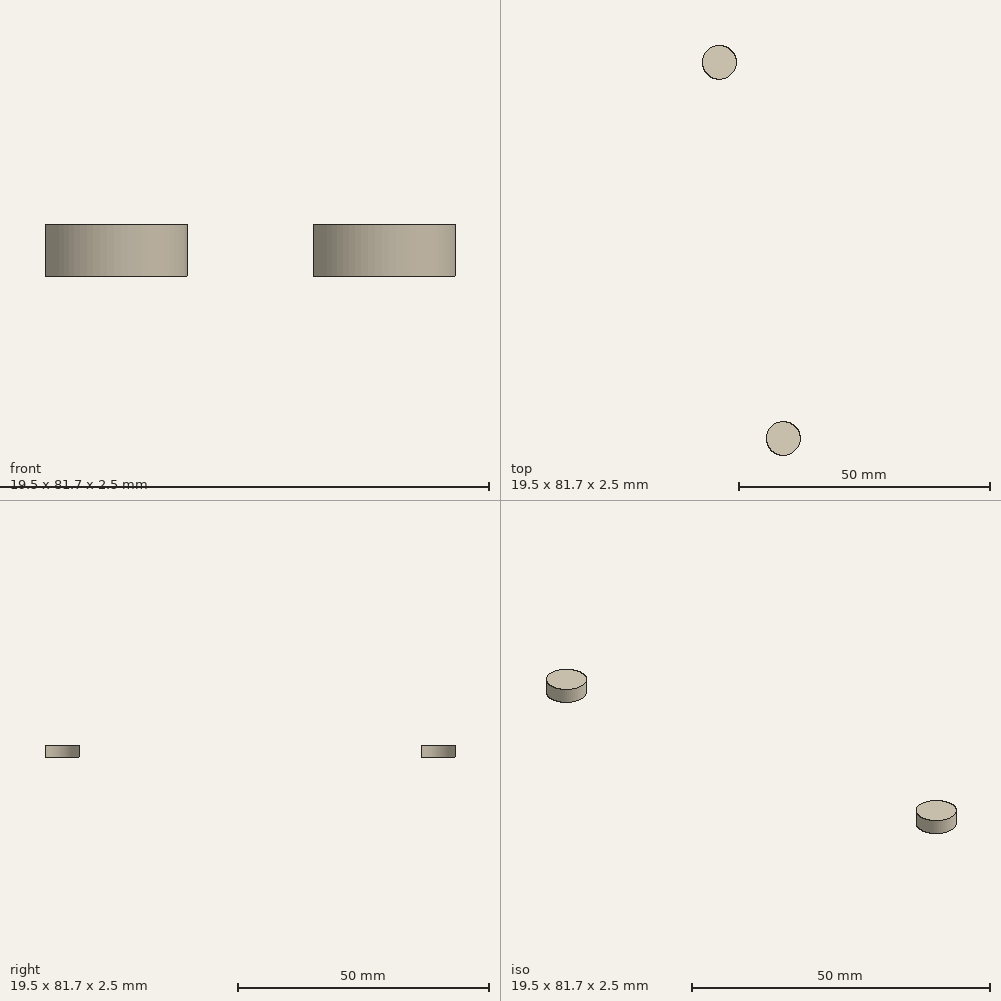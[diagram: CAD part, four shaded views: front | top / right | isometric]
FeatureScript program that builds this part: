
annotation { "Feature Type Name" : "Feature", "Feature Type Description" : "" }
export const myFeature = defineFeature(function(context is Context, id is Id, definition is map)
    precondition{}
    {
        {
            var Q0;
            Q0=qCreatedBy(makeId("Top.planeOp"),FACE);
            var sketch = newSketch(context, id + "F0", { "sketchPlane" : qUnion([Q0])});
            skLineSegment(sketch, "E0", {"start": v(0, 60) * mm, "end": v(0, -60) * mm});
            skLineSegment(sketch, "E1", {"start": v(-70, 0) * mm, "end": v(70, 0) * mm});
            skCircle(sketch, "E2", {"center": v(-12.25, -50) * mm, "radius": 3.37 * mm});
            skCircle(sketch, "E3", {"center": v(12.25, -50) * mm, "radius": 3.37 * mm});
            skCircle(sketch, "E4", {"center": v(-25, -25) * mm, "radius": 3.37 * mm});
            skCircle(sketch, "E5", {"center": v(-25, 0) * mm, "radius": 3.37 * mm});
            skCircle(sketch, "E6", {"center": v(-25, 25) * mm, "radius": 3.37 * mm});
            skCircle(sketch, "E7", {"center": v(-25, 50) * mm, "radius": 3.37 * mm});
            skCircle(sketch, "E8", {"center": v(25, -25) * mm, "radius": 3.37 * mm});
            skCircle(sketch, "E9", {"center": v(25, 0) * mm, "radius": 3.37 * mm});
            skCircle(sketch, "E10", {"center": v(25, 25) * mm, "radius": 3.37 * mm});
            skCircle(sketch, "E11", {"center": v(25, 50) * mm, "radius": 3.37 * mm});
            skLineSegment(sketch, "E12", {"start": v(50, -75) * mm, "end": v(-50, -75) * mm});
            skLineSegment(sketch, "E13", {"start": v(-50, 75) * mm, "end": v(-50, -75) * mm});
            skLineSegment(sketch, "E14", {"start": v(-50, 75) * mm, "end": v(50, 75) * mm});
            skLineSegment(sketch, "E15", {"start": v(50, 75) * mm, "end": v(50, -75) * mm});
            skSolve(sketch);
        }
        {
            var Q0;
            Q0=makeQuery(id+"F0.imprint","IMPRINT",FACE,{"disambiguationData":[TD([[makeQuery(id+"F0.imprint","IMPRINT",EDGE,{"derivedFrom":sQuery(id+"F0.wireOp",EDGE,"E6")}),1.0]])]});
            var Q1;
            Q1=makeQuery(id+"F0.imprint","IMPRINT",FACE,{"disambiguationData":[TD([[makeQuery(id+"F0.imprint","IMPRINT",EDGE,{"derivedFrom":sQuery(id+"F0.wireOp",EDGE,"E2")}),1.0]])]});
            extrude(context, id + "F1", {"entities" : qUnion([Q0, Q1]), "depth" : 2.5 * mm});
        }
    });
